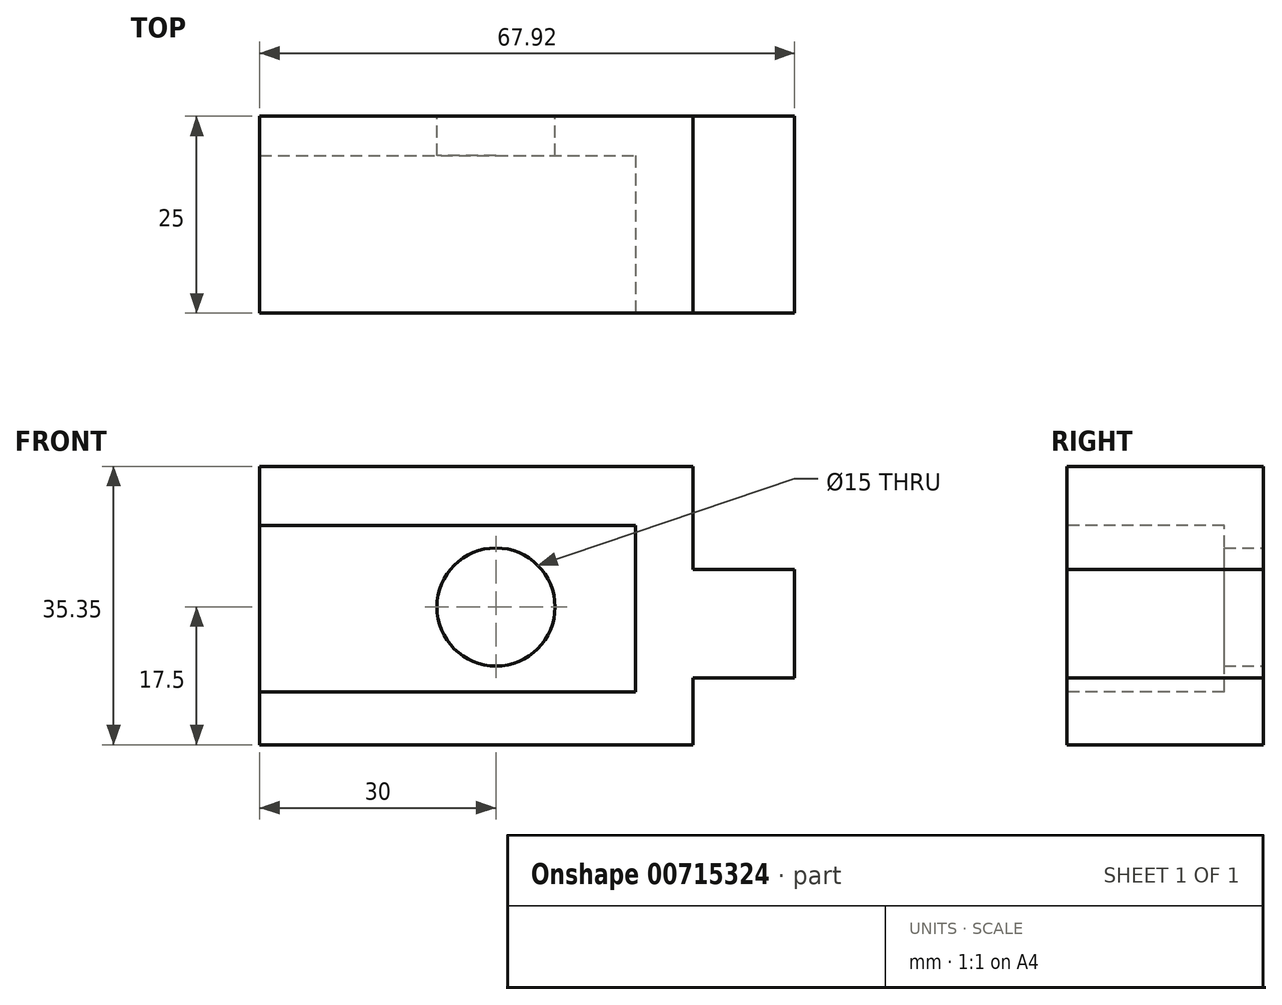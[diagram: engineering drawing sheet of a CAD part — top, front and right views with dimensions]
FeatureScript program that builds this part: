
annotation { "Feature Type Name" : "Feature", "Feature Type Description" : "" }
export const myFeature = defineFeature(function(context is Context, id is Id, definition is map)
    precondition{}
    {
        {
            var Q0;
            Q0=qCreatedBy(makeId("Front.planeOp"),FACE);
            var sketch = newSketch(context, id + "F0", { "sketchPlane" : qUnion([Q0])});
            skLineSegment(sketch, "E0.bottom", {"start": v(0, 0) * mm, "end": v(55.04, 0) * mm});
            skLineSegment(sketch, "E0.top", {"start": v(0, 35.35) * mm, "end": v(55.04, 35.35) * mm});
            skLineSegment(sketch, "E0.left", {"start": v(0, 0) * mm, "end": v(0, 35.35) * mm});
            skLineSegment(sketch, "E0.right", {"start": v(55.04, 0) * mm, "end": v(55.04, 35.35) * mm});
            skLineSegment(sketch, "E1.bottom", {"start": v(67.92, 22.28) * mm, "end": v(42.87, 22.28) * mm});
            skLineSegment(sketch, "E1.top", {"start": v(67.92, 8.5) * mm, "end": v(42.87, 8.5) * mm});
            skLineSegment(sketch, "E1.left", {"start": v(67.92, 22.28) * mm, "end": v(67.92, 8.5) * mm});
            skLineSegment(sketch, "E1.right", {"start": v(42.87, 22.28) * mm, "end": v(42.87, 8.5) * mm});
            skSolve(sketch);
        }
        {
            var Q0;
            Q0 = qSketchRegion(id + "F0", true);
            extrude(context, id + "F1", {"entities" : qUnion([Q0]), "depth" : 25 * mm, "offsetDistance" : 25 * mm});
        }
        {
            var Q0;
            Q0=makeQuery(id+"F1.opExtrude","CAP_FACE",FACE,{"disambiguationData":[OSD([sQuery(id+"F0.wireOp",EDGE,"E0.bottom"),sQuery(id+"F0.wireOp",EDGE,"E0.top"),sQuery(id+"F0.wireOp",EDGE,"E0.left"),sQuery(id+"F0.wireOp",EDGE,"E0.right"),sQuery(id+"F0.wireOp",EDGE,"E1.bottom"),sQuery(id+"F0.wireOp",EDGE,"E1.top"),sQuery(id+"F0.wireOp",EDGE,"E1.left")])],"isStart":false});
            var sketch = newSketch(context, id + "F2", { "sketchPlane" : qUnion([Q0])});
            skLineSegment(sketch, "E2.bottom", {"start": v(0, 27.83) * mm, "end": v(47.7, 27.83) * mm});
            skLineSegment(sketch, "E2.top", {"start": v(0, 6.71) * mm, "end": v(47.7, 6.71) * mm});
            skLineSegment(sketch, "E2.left", {"start": v(0, 27.83) * mm, "end": v(0, 6.71) * mm});
            skLineSegment(sketch, "E2.right", {"start": v(47.7, 27.83) * mm, "end": v(47.7, 6.71) * mm});
            skSolve(sketch);
        }
        {
            var Q0;
            Q0 = qSketchRegion(id + "F2", true);
            extrude(context, id + "F3", {"entities" : qUnion([Q0]), "operationType" : NewBodyOperationType.REMOVE, "oppositeDirection" : true, "depth" : 20 * mm, "offsetDistance" : 25 * mm});
        }
        {
            var Q0;
            Q0=makeQuery(id+"F1.opExtrude","CAP_FACE",FACE,{"disambiguationData":[OSD([sQuery(id+"F0.wireOp",EDGE,"E0.bottom"),sQuery(id+"F0.wireOp",EDGE,"E0.top"),sQuery(id+"F0.wireOp",EDGE,"E0.left"),sQuery(id+"F0.wireOp",EDGE,"E0.right"),sQuery(id+"F0.wireOp",EDGE,"E1.bottom"),sQuery(id+"F0.wireOp",EDGE,"E1.top"),sQuery(id+"F0.wireOp",EDGE,"E1.left")])],"isStart":true});
            var sketch = newSketch(context, id + "F4", { "sketchPlane" : qUnion([Q0])});
            skCircle(sketch, "E3", {"center": v(-30, 17.5) * mm, "radius": 7.5 * mm});
            skSolve(sketch);
        }
        {
            var Q0;
            Q0 = qSketchRegion(id + "F4", true);
            extrude(context, id + "F5", {"entities" : qUnion([Q0]), "operationType" : NewBodyOperationType.REMOVE, "oppositeDirection" : true, "depth" : 25 * mm, "offsetDistance" : 25 * mm});
        }
    });
